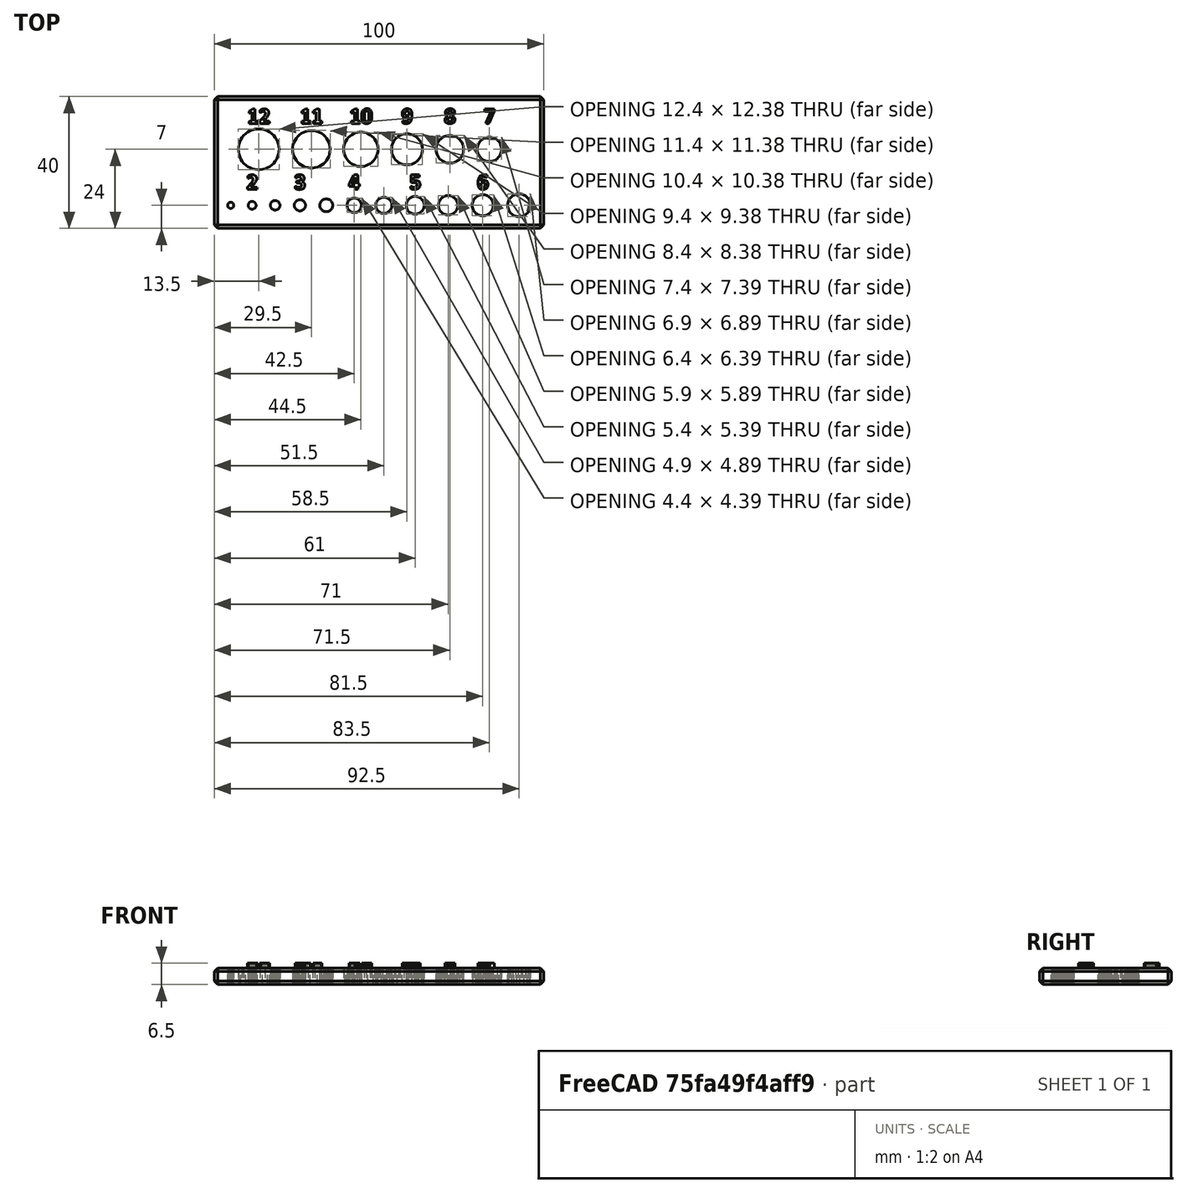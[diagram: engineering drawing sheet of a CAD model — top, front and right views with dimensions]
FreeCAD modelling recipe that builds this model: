
FCSTD DOCUMENT  (FreeCAD 0.19R23463 (Git))
Label: measurement tool
License: All rights reserved
LicenseURL: http://en.wikipedia.org/wiki/All_rights_reserved
objects: Part::Feature×2, Mesh::Feature×1, Part::Refine×1, Part::Chamfer×1
note: 4 computed .brp shape members not serialized (recipe doc carries the construction recipe); baked Part::Feature solids carry a one-line shape summary decoded from their .brp

FEATURE [Mesh::Feature] measurement_tool  label="measurement tool"
FEATURE [Part::Feature] measurement_tool001
  shape: bbox 100 x 40 x 6.5 mm, 10864 faces, 0 solids (baked)
FEATURE [Part::Feature] measurement_tool001_solid  label="measurement_tool001 (Solid)"
  shape: bbox 100 x 40 x 6.5 mm, 10864 faces (baked)
FEATURE [Part::Refine] measurement_tool001_solid001  label="measurement_tool001 (Solid)001"
  Source = -> measurement_tool001_solid
FEATURE [Part::Chamfer] Chamfer
  Base = -> measurement_tool001_solid001
  Edges = 12 edges r=1: [Edge112,Edge113,Edge114,Edge115,Edge4352,Edge4353,Edge4354,Edge4355,Edge6053,Edge6054,Edge6055,Edge6056]
